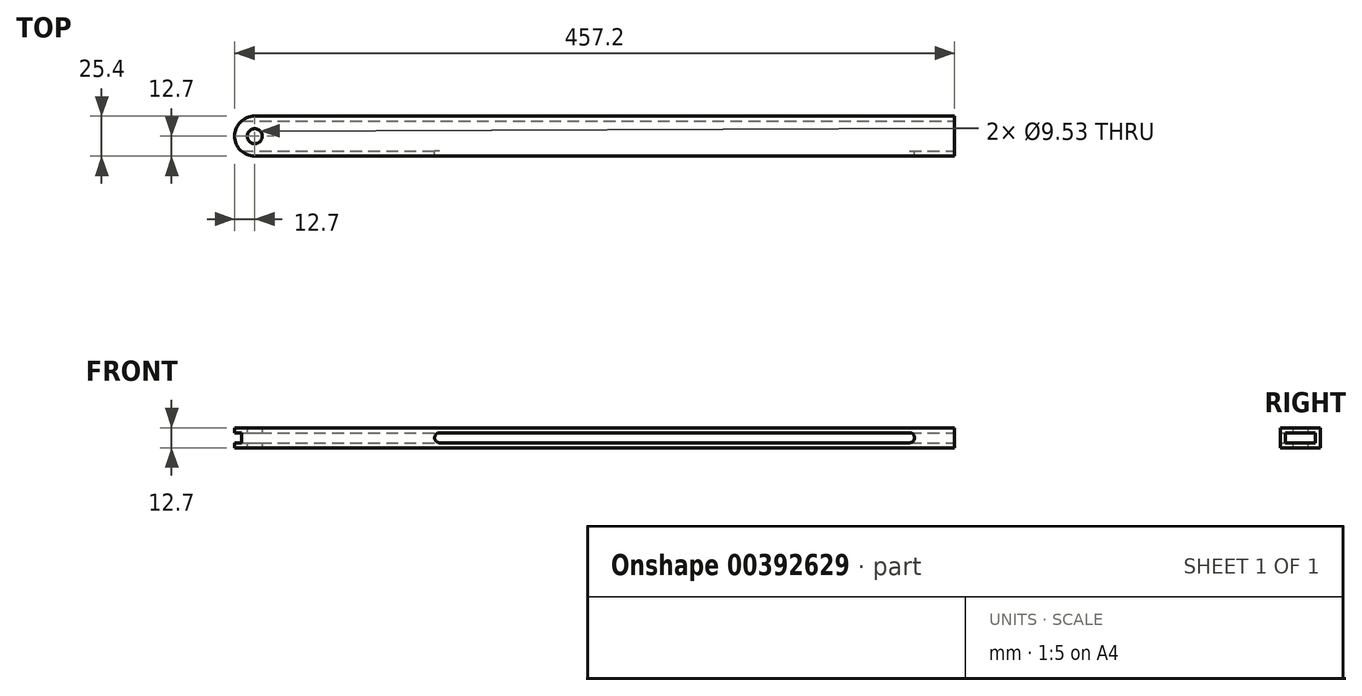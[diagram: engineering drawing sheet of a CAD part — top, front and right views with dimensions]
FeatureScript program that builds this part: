
annotation { "Feature Type Name" : "Feature", "Feature Type Description" : "" }
export const myFeature = defineFeature(function(context is Context, id is Id, definition is map)
    precondition{}
    {
        {
            var Q0;
            Q0=qCreatedBy(makeId("Top.planeOp"),FACE);
            var sketch = newSketch(context, id + "F0", { "sketchPlane" : qUnion([Q0])});
            skLineSegment(sketch, "E0.bottom", {"start": v(-228.6, 12.7) * mm, "end": v(228.6, 12.7) * mm});
            skLineSegment(sketch, "E0.top", {"start": v(-228.6, -12.7) * mm, "end": v(228.6, -12.7) * mm});
            skLineSegment(sketch, "E0.left", {"start": v(-228.6, 12.7) * mm, "end": v(-228.6, -12.7) * mm});
            skLineSegment(sketch, "E0.right", {"start": v(228.6, 12.7) * mm, "end": v(228.6, -12.7) * mm});
            skPoint(sketch, "E0.middle", {"position": v(0, 0) * mm});
            skSolve(sketch);
        }
        {
            var Q0;
            Q0=makeQuery(id+"F0.imprint","IMPRINT",FACE,{"disambiguationData":[TD([[makeQuery(id+"F0.imprint","IMPRINT",EDGE,{"derivedFrom":sQuery(id+"F0.wireOp",EDGE,"E0.bottom")}),-1.0]])]});
            extrude(context, id + "F1", {"entities" : qUnion([Q0]), "endBound" : BoundingType.SYMMETRIC, "depth" : 12.7 * mm});
        }
        {
            var Q0;
            Q0=makeQuery(id+"F1.opExtrude","SWEPT_EDGE",EDGE,{"disambiguationData":[OSD([sQuery(id+"F0.wireOp",EDGE,"E0.bottom"),sQuery(id+"F0.wireOp",EDGE,"E0.left")])]});
            var Q1;
            Q1=makeQuery(id+"F1.opExtrude","SWEPT_EDGE",EDGE,{"disambiguationData":[OSD([sQuery(id+"F0.wireOp",EDGE,"E0.top"),sQuery(id+"F0.wireOp",EDGE,"E0.left")])]});
            fillet(context, id + "F2", {"entities" : qUnion([Q0, Q1]), "radius" : 12.7 * mm, "tangentPropagation" : true, "allowEdgeOverflow" : false});
        }
        {
            var Q0;
            Q0=makeQuery(id+"F1.opExtrude","CAP_FACE",FACE,{"disambiguationData":[OSD([sQuery(id+"F0.wireOp",EDGE,"E0.bottom"),sQuery(id+"F0.wireOp",EDGE,"E0.top"),sQuery(id+"F0.wireOp",EDGE,"E0.left"),sQuery(id+"F0.wireOp",EDGE,"E0.right")])],"isStart":true});
            var sketch = newSketch(context, id + "F3", { "sketchPlane" : qUnion([Q0])});
            skCircle(sketch, "E1", {"center": v(-215.9, 0) * mm, "radius": 4.76 * mm});
            skSolve(sketch);
        }
        {
            var Q0;
            Q0 = qSketchRegion(id + "F3", true);
            extrude(context, id + "F4", {"entities" : qUnion([Q0]), "operationType" : NewBodyOperationType.REMOVE, "endBound" : BoundingType.THROUGH_ALL, "oppositeDirection" : true, "depth" : 25.4 * mm});
        }
        {
            var Q0;
            Q0=qCreatedBy(makeId("Right.planeOp"),FACE);
            var sketch = newSketch(context, id + "F5", { "sketchPlane" : qUnion([Q0])});
            skLineSegment(sketch, "E2.bottom", {"start": v(-9.52, -3.18) * mm, "end": v(9.53, -3.18) * mm});
            skLineSegment(sketch, "E2.top", {"start": v(-9.52, 3.17) * mm, "end": v(9.52, 3.17) * mm});
            skLineSegment(sketch, "E2.left", {"start": v(-9.53, -3.18) * mm, "end": v(-9.53, 3.17) * mm});
            skLineSegment(sketch, "E2.right", {"start": v(9.53, -3.18) * mm, "end": v(9.53, 3.17) * mm});
            skPoint(sketch, "E2.middle", {"position": v(0, 0) * mm});
            skSolve(sketch);
        }
        {
            var Q0;
            Q0 = qSketchRegion(id + "F5", true);
            extrude(context, id + "F6", {"entities" : qUnion([Q0]), "operationType" : NewBodyOperationType.REMOVE, "endBound" : BoundingType.THROUGH_ALL, "oppositeDirection" : true, "depth" : 25.4 * mm, "hasSecondDirection" : true, "secondDirectionBound" : SecondDirectionBoundingType.THROUGH_ALL, "secondDirectionOppositeDirection" : false, "secondDirectionDepth" : 25.4 * mm});
        }
        {
            var Q0;
            Q0=qCreatedBy(makeId("Front.planeOp"),FACE);
            var sketch = newSketch(context, id + "F7", { "sketchPlane" : qUnion([Q0])});
            skLineSegment(sketch, "E3.bottom", {"start": v(-101.6, -3.18) * mm, "end": v(203.2, -3.18) * mm});
            skLineSegment(sketch, "E3.top", {"start": v(-101.6, 3.18) * mm, "end": v(203.2, 3.18) * mm});
            skLineSegment(sketch, "E3.left", {"start": v(-101.6, -3.17) * mm, "end": v(-101.6, 3.17) * mm});
            skLineSegment(sketch, "E3.right", {"start": v(203.2, -3.17) * mm, "end": v(203.2, 3.17) * mm});
            skPoint(sketch, "E3.middle", {"position": v(50.8, 0) * mm});
            skPoint(sketch, "E4.endSnap0", {"position": v(203.2, 0) * mm});
            skLineSegment(sketch, "E5", {"start": v(203.2, 0) * mm, "end": v(228.6, 0) * mm, "construction": true});
            skSolve(sketch);
        }
        {
            var Q0;
            Q0 = qSketchRegion(id + "F7", true);
            extrude(context, id + "F8", {"entities" : qUnion([Q0]), "operationType" : NewBodyOperationType.REMOVE, "endBound" : BoundingType.THROUGH_ALL, "depth" : 3.17 * mm});
        }
        {
            var Q0;
            Q0=makeQuery(id+"F8.boolean.opBoolean","COPY",EDGE,{"derivedFrom":makeQuery(id+"F8.opExtrude","SWEPT_EDGE",EDGE,{"disambiguationData":[OSD([sQuery(id+"F7.wireOp",EDGE,"E3.top"),sQuery(id+"F7.wireOp",EDGE,"E3.left")])]})});
            var Q1;
            Q1=makeQuery(id+"F8.boolean.opBoolean","COPY",EDGE,{"derivedFrom":makeQuery(id+"F8.opExtrude","SWEPT_EDGE",EDGE,{"disambiguationData":[OSD([sQuery(id+"F7.wireOp",EDGE,"E3.bottom"),sQuery(id+"F7.wireOp",EDGE,"E3.right")])]})});
            var Q2;
            Q2=makeQuery(id+"F8.boolean.opBoolean","COPY",EDGE,{"derivedFrom":makeQuery(id+"F8.opExtrude","SWEPT_EDGE",EDGE,{"disambiguationData":[OSD([sQuery(id+"F7.wireOp",EDGE,"E3.top"),sQuery(id+"F7.wireOp",EDGE,"E3.right")])]})});
            var Q3;
            Q3=makeQuery(id+"F8.boolean.opBoolean","COPY",EDGE,{"derivedFrom":makeQuery(id+"F8.opExtrude","SWEPT_EDGE",EDGE,{"disambiguationData":[OSD([sQuery(id+"F7.wireOp",EDGE,"E3.bottom"),sQuery(id+"F7.wireOp",EDGE,"E3.left")])]})});
            fillet(context, id + "F9", {"entities" : qUnion([Q0, Q1, Q2, Q3]), "radius" : 3.17 * mm, "tangentPropagation" : true, "allowEdgeOverflow" : false});
        }
    });
